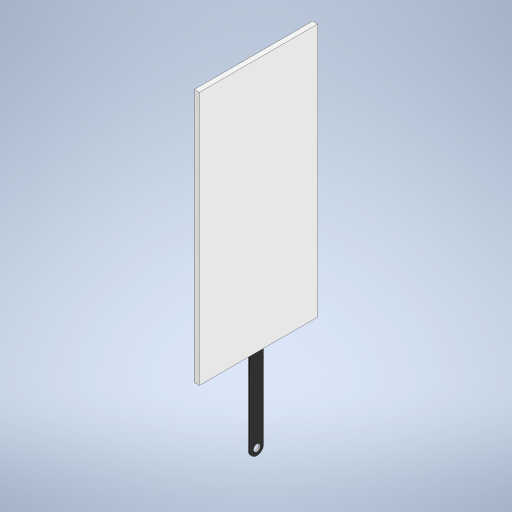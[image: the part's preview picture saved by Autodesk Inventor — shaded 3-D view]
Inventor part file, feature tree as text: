
AUTODESK INVENTOR PART (.ipt)
format: ipt  version: 2023 (Build 270158000, 158)  size: 252,928 bytes
history: native  units: mm
features: extrude x2, sketch x2, other x1
ambient origin geometry x8: Origin, YZ Plane, XZ Plane, XY Plane, X Axis, Y Axis, Z Axis, Center Point
bodies: Body1 (feature_tree)
feature tree (5):
  other  "Bryła1"
  extrude  "Wyciągnięcie proste1"  Depth=8.0mm
  extrude  "Wyciągnięcie proste2"  Depth=4.0mm
  sketch  "Szkic1"
  sketch  "Szkic2"
